# Revit family: Curtain_wall_folding_doors_11229_2
name_source: partatom
category: Curtain Panels
revit_build: Autodesk Revit 2014 (Build: 20131024_2115(x64)
units: mm (PartAtom-declared; Revit-internal decimal feet)

## types (1)
- Curtain_wall_folding_doors_11229_2
    Frame depth = 150 mm
    Frame material = Frame material
    Frame thickness = 50 mm  [stored 0.164042 ft]
    Glass material = Glass
    Glass thickness = 20 mm  [stored 0.0656168 ft]
    Left 1 = No
    Left 2 = No
    Left 3 = No
    Left 4 = No
    Left 5 = No
    No of left panels = 0
    No of right panels = 3
    Offset = 60 mm
    Open angle = 80.00°
    Panel bottom rail width = 150 mm
    Panel frame material = Frame material
    Panel mullion width = 50 mm  [stored 0.164042 ft]
    Panel thickness = 40 mm  [stored 0.131234 ft]
    Panel top rail width = 100 mm  [stored 0.328084 ft]
    Right 1 = Yes
    Right 2 = Yes
    Right 3 = Yes
    Right 4 = No
    Right 5 = No

note: [stored X ft] marks values corroborated as IEEE doubles in the binary element streams (Revit-internal decimal feet)

## geometry (parser evidence)
native form markers: Sweep x7
no freeform markers — native parametric forms only
